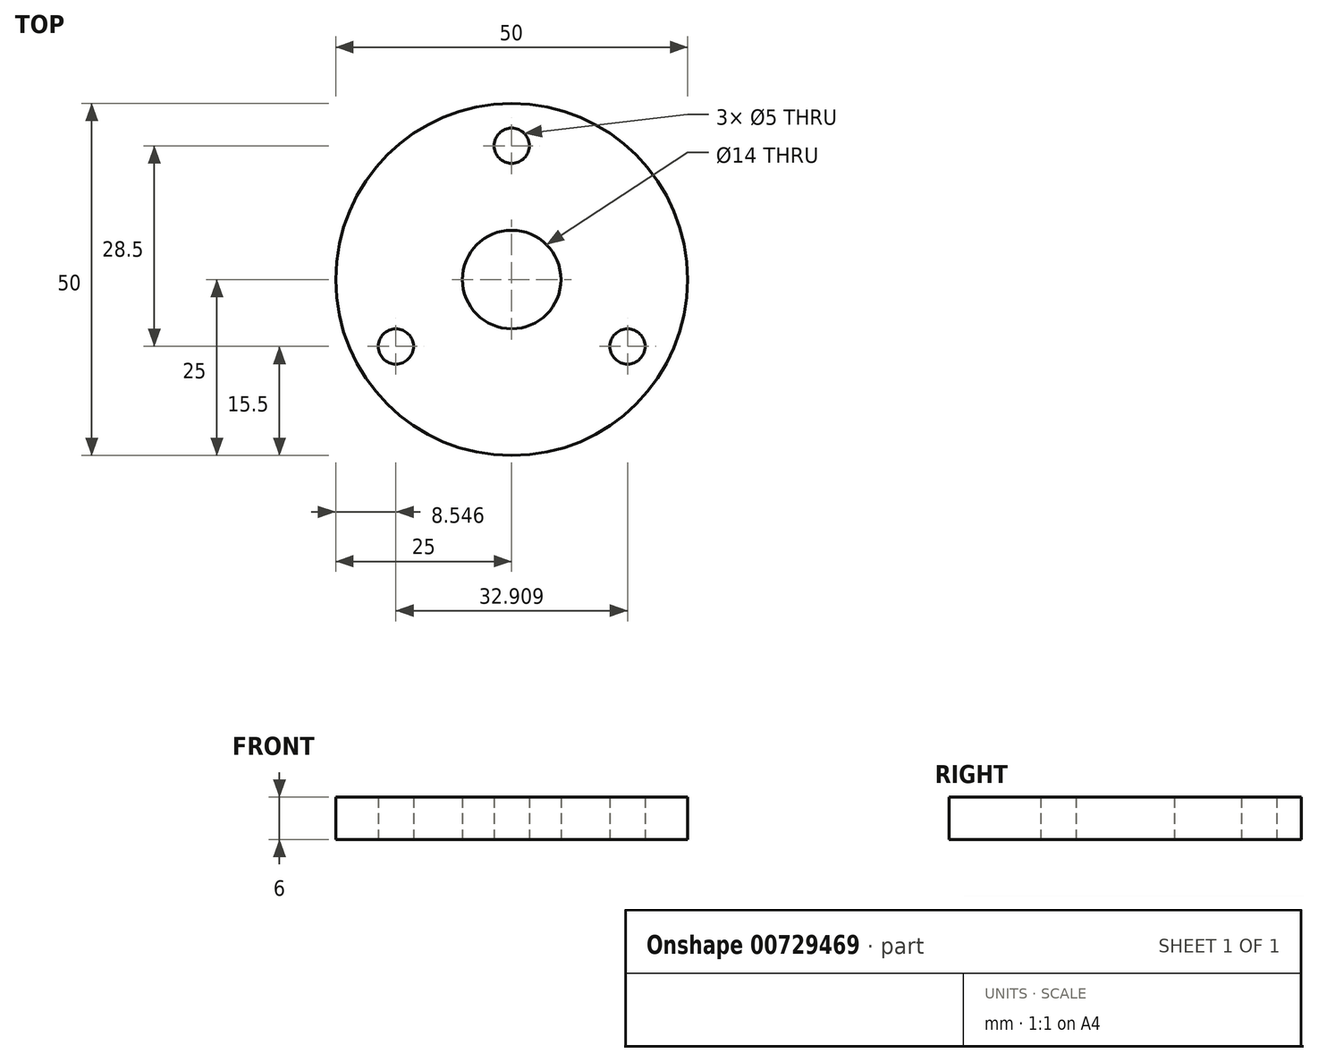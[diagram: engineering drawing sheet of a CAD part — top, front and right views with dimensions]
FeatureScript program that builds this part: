
annotation { "Feature Type Name" : "Feature", "Feature Type Description" : "" }
export const myFeature = defineFeature(function(context is Context, id is Id, definition is map)
    precondition{}
    {
        {
            var Q0;
            Q0=qCreatedBy(makeId("Top.planeOp"),FACE);
            var sketch = newSketch(context, id + "F0", { "sketchPlane" : qUnion([Q0])});
            skCircle(sketch, "E0", {"center": v(0, 0) * mm, "radius": 25 * mm});
            skCircle(sketch, "E1", {"center": v(0, 0) * mm, "radius": 7 * mm});
            skCircle(sketch, "E2.cCircle", {"center": v(0, 0) * mm, "radius": 19 * mm, "construction": true});
            skCircle(sketch, "E3", {"center": v(0, 19) * mm, "radius": 2.5 * mm});
            skCircle(sketch, "E4", {"center": v(-16.45, -9.5) * mm, "radius": 2.5 * mm});
            skCircle(sketch, "E5", {"center": v(16.45, -9.5) * mm, "radius": 2.5 * mm});
            skSolve(sketch);
        }
        {
            var Q0;
            Q0=qCreatedBy(makeId("Top.planeOp"),FACE);
            var sketch = newSketch(context, id + "F1", { "sketchPlane" : qUnion([Q0])});
            skCircle(sketch, "E6", {"center": v(0, 0) * mm, "radius": 25 * mm});
            skCircle(sketch, "E7", {"center": v(0, 0) * mm, "radius": 7 * mm});
            skCircle(sketch, "E8.cCircle", {"center": v(0, 0) * mm, "radius": 19 * mm, "construction": true});
            skLineSegment(sketch, "E8.0", {"start": v(0, 19) * mm, "end": v(16.45, -9.5) * mm, "construction": true});
            skLineSegment(sketch, "E8.1", {"start": v(16.45, -9.5) * mm, "end": v(-16.45, -9.5) * mm, "construction": true});
            skLineSegment(sketch, "E8.2", {"start": v(-16.45, -9.5) * mm, "end": v(0, 19) * mm, "construction": true});
            skCircle(sketch, "E9", {"center": v(0, 19) * mm, "radius": 2.5 * mm});
            skCircle(sketch, "E10", {"center": v(-16.4, -9.49) * mm, "radius": 2.5 * mm});
            skCircle(sketch, "E11", {"center": v(16.6, -9.35) * mm, "radius": 2.5 * mm});
            skSolve(sketch);
        }
        {
            var Q0;
            Q0=qCreatedBy(makeId("Top.planeOp"),FACE);
            var sketch = newSketch(context, id + "F2", { "sketchPlane" : qUnion([Q0])});
            skCircle(sketch, "E12", {"center": v(0, 0) * mm, "radius": 25 * mm});
            skCircle(sketch, "E13", {"center": v(0, 0) * mm, "radius": 7 * mm});
            skCircle(sketch, "E14", {"center": v(0, 19) * mm, "radius": 2.5 * mm});
            skCircle(sketch, "E15", {"center": v(-16.45, -9.5) * mm, "radius": 2.5 * mm});
            skCircle(sketch, "E16", {"center": v(16.45, -9.5) * mm, "radius": 2.5 * mm});
            skLineSegment(sketch, "E17", {"start": v(0, 0) * mm, "end": v(16.45, -9.5) * mm, "construction": true});
            skLineSegment(sketch, "E18", {"start": v(-16.45, -9.5) * mm, "end": v(0, 0) * mm, "construction": true});
            skSolve(sketch);
        }
        {
            var Q0;
            Q0=makeQuery(id+"F2.imprint","IMPRINT",FACE,{"disambiguationData":[TD([[makeQuery(id+"F2.imprint","IMPRINT",EDGE,{"derivedFrom":sQuery(id+"F2.wireOp",EDGE,"E12")}),1.0]])]});
            extrude(context, id + "F3", {"entities" : qUnion([Q0]), "depth" : 6 * mm, "offsetDistance" : 25 * mm});
        }
    });
